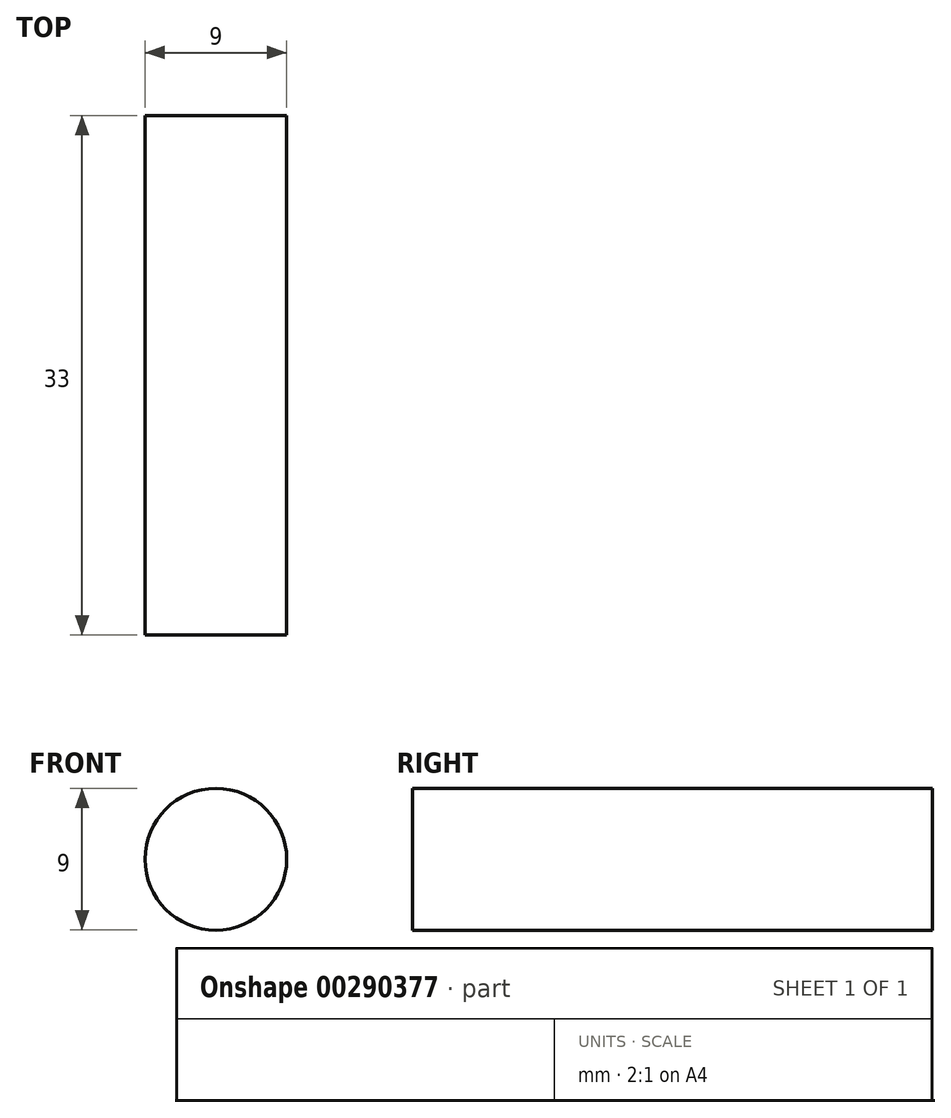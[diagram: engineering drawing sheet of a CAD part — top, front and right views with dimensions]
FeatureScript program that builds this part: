
annotation { "Feature Type Name" : "Feature", "Feature Type Description" : "" }
export const myFeature = defineFeature(function(context is Context, id is Id, definition is map)
    precondition{}
    {
        {
            var Q0;
            Q0=qCreatedBy(makeId("Front.planeOp"),FACE);
            var sketch = newSketch(context, id + "F0", { "sketchPlane" : qUnion([Q0])});
            skCircle(sketch, "E0", {"center": v(-24.97, 20.5) * mm, "radius": 4.5 * mm});
            skSolve(sketch);
        }
        {
            var Q0;
            Q0=makeQuery(id+"F0.imprint","IMPRINT",FACE,{"disambiguationData":[TD([[makeQuery(id+"F0.imprint","IMPRINT",EDGE,{"derivedFrom":sQuery(id+"F0.wireOp",EDGE,"E0")}),1.0]])]});
            var Q1;
            Q1=sQuery(id+"F0.wireOp",EDGE,"E0");
            extrude(context, id + "F1", {"entities" : qUnion([Q0]), "surfaceEntities" : qUnion([Q1]), "depth" : 33 * mm});
        }
    });
